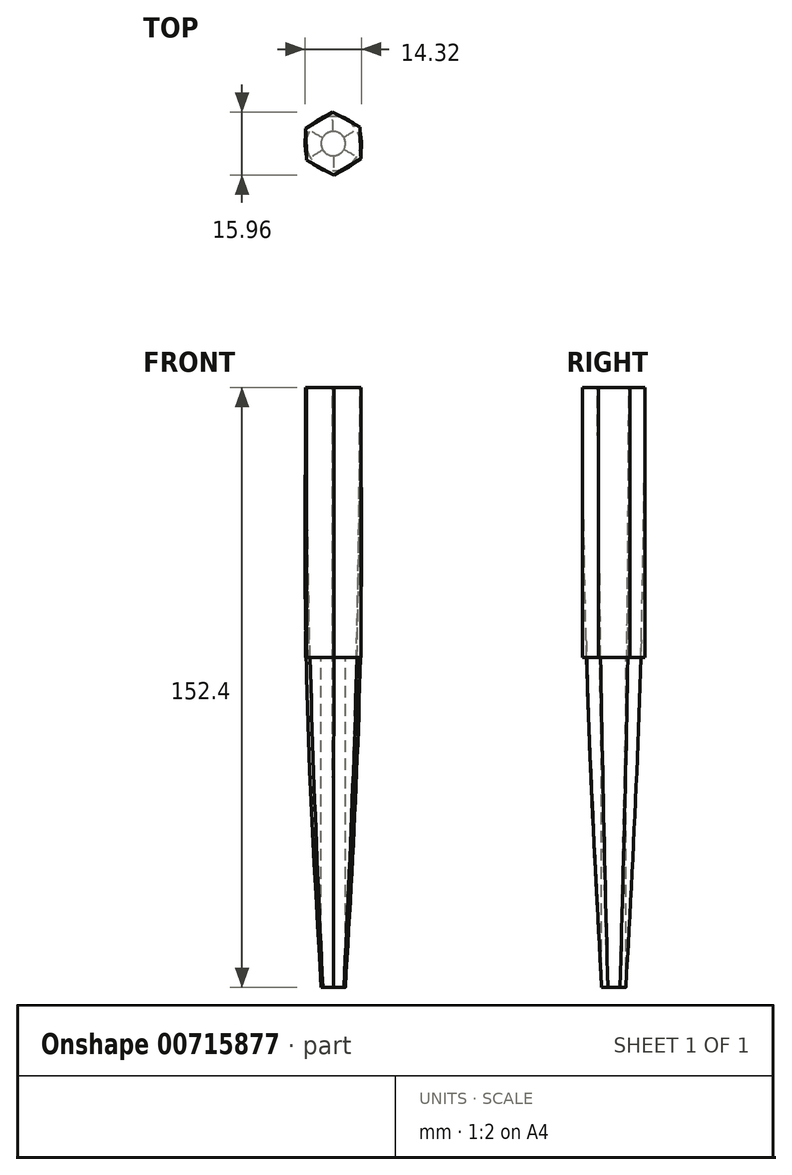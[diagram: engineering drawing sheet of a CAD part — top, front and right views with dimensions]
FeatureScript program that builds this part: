
annotation { "Feature Type Name" : "Feature", "Feature Type Description" : "" }
export const myFeature = defineFeature(function(context is Context, id is Id, definition is map)
    precondition{}
    {
        {
            var Q0;
            Q0=qCreatedBy(makeId("Top.planeOp"),FACE);
            var sketch = newSketch(context, id + "F0", { "sketchPlane" : qUnion([Q0])});
            skCircle(sketch, "E0.cCircle", {"center": v(0, 0) * mm, "radius": 6.91 * mm, "construction": true});
            skLineSegment(sketch, "E0.0", {"start": v(6.83, 4.14) * mm, "end": v(7, -3.84) * mm});
            skLineSegment(sketch, "E0.1", {"start": v(7, -3.84) * mm, "end": v(0.17, -7.98) * mm});
            skLineSegment(sketch, "E0.2", {"start": v(0.17, -7.98) * mm, "end": v(-6.83, -4.14) * mm});
            skLineSegment(sketch, "E0.3", {"start": v(-6.83, -4.14) * mm, "end": v(-7, 3.84) * mm});
            skLineSegment(sketch, "E0.4", {"start": v(-7, 3.84) * mm, "end": v(-0.17, 7.98) * mm});
            skLineSegment(sketch, "E0.5", {"start": v(-0.17, 7.98) * mm, "end": v(6.83, 4.14) * mm});
            skPoint(sketch, "E0.0.midPoint", {"position": v(6.91, 0.15) * mm});
            skSolve(sketch);
        }
        {
            var Q0;
            Q0=makeQuery(id+"F0.imprint","IMPRINT",FACE,{"disambiguationData":[TD([[makeQuery(id+"F0.imprint","IMPRINT",EDGE,{"derivedFrom":sQuery(id+"F0.wireOp",EDGE,"E0.0")}),-1.0]])]});
            extrude(context, id + "F1", {"entities" : qUnion([Q0]), "depth" : 68.58 * mm, "offsetDistance" : 25.4 * mm});
        }
        {
            var Q0;
            Q0=qCreatedBy(makeId("Top.planeOp"),FACE);
            var sketch = newSketch(context, id + "F2", { "sketchPlane" : qUnion([Q0])});
            skCircle(sketch, "E1", {"center": v(0, 0) * mm, "radius": 3.1 * mm});
            skSolve(sketch);
        }
        {
            var Q0;
            Q0=makeQuery(id+"F2.imprint","IMPRINT",FACE,{"disambiguationData":[TD([[makeQuery(id+"F2.imprint","IMPRINT",EDGE,{"derivedFrom":sQuery(id+"F2.wireOp",EDGE,"E1")}),1.0]])]});
            extrude(context, id + "F3", {"entities" : qUnion([Q0]), "oppositeDirection" : true, "depth" : 83.82 * mm, "offsetDistance" : 25.4 * mm});
        }
        {
            var Q0;
            Q0=qCreatedBy(makeId("Top.planeOp"),FACE);
            var sketch = newSketch(context, id + "F4", { "sketchPlane" : qUnion([Q0])});
            skCircle(sketch, "E2", {"center": v(0, 0) * mm, "radius": 6.88 * mm});
            skSolve(sketch);
        }
        {
            var Q0;
            Q0 = qSketchRegion(id + "F4", true);
            extrude(context, id + "F5", {"entities" : qUnion([Q0]), "depth" : 0.03 * mm, "offsetDistance" : 25.4 * mm});
        }
        {
            var Q0;
            Q0=makeQuery(id+"F3.opExtrude","CAP_FACE",FACE,{"disambiguationData":[OSD([sQuery(id+"F2.wireOp",EDGE,"E1")])],"isStart":false});
            var Q1;
            Q1=makeQuery(id+"F5.opExtrude","CAP_FACE",FACE,{"disambiguationData":[OSD([sQuery(id+"F4.wireOp",EDGE,"E2")])],"isStart":true});
            var Q2;
            Q2=makeQuery(id+"F1.opExtrude","CAP_FACE",FACE,{"disambiguationData":[OSD([sQuery(id+"F0.wireOp",EDGE,"E0.0"),sQuery(id+"F0.wireOp",EDGE,"E0.1"),sQuery(id+"F0.wireOp",EDGE,"E0.2"),sQuery(id+"F0.wireOp",EDGE,"E0.3"),sQuery(id+"F0.wireOp",EDGE,"E0.4"),sQuery(id+"F0.wireOp",EDGE,"E0.5")])],"isStart":false});
            loft(context, id + "F6", {"sheetProfilesArray" : [{ "sheetProfileEntities" : qUnion([Q0]) }, { "sheetProfileEntities" : qUnion([Q1]) }, { "sheetProfileEntities" : qUnion([Q2]) }]});
        }
    });
